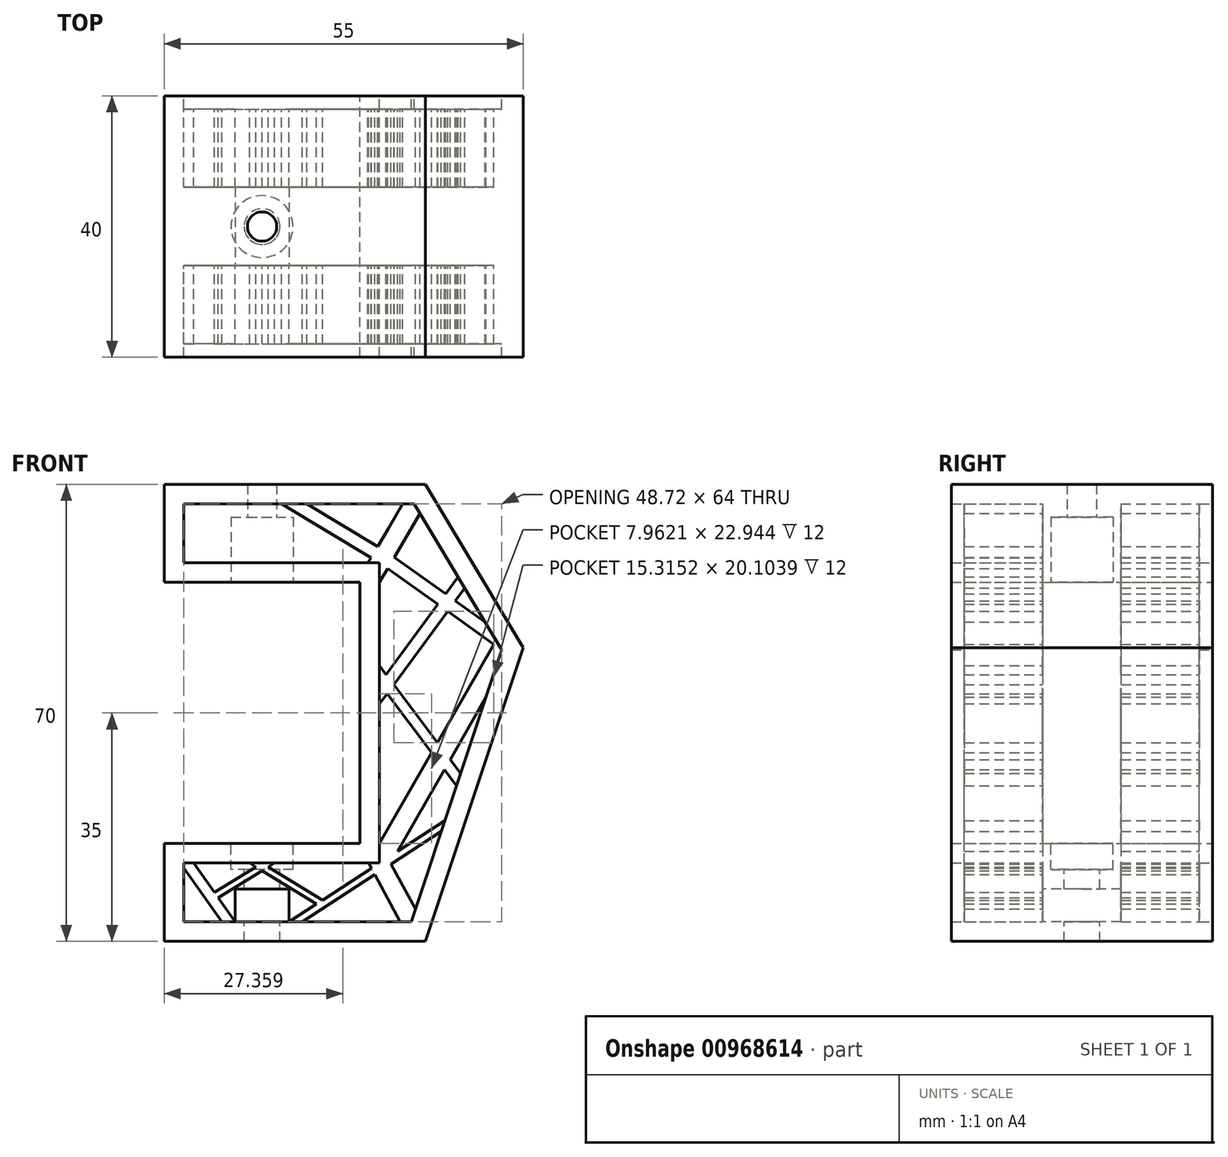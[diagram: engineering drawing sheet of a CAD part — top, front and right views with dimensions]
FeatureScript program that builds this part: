
annotation { "Feature Type Name" : "Feature", "Feature Type Description" : "" }
export const myFeature = defineFeature(function(context is Context, id is Id, definition is map)
    precondition{}
    {
        {
            var Q0;
            Q0=qCreatedBy(makeId("Front.planeOp"),FACE);
            var sketch = newSketch(context, id + "F0", { "sketchPlane" : qUnion([Q0])});
            skLineSegment(sketch, "E0", {"start": v(0, 21.86) * mm, "end": v(-30, 21.86) * mm});
            skLineSegment(sketch, "E1", {"start": v(-30, 21.86) * mm, "end": v(-30, 36.86) * mm});
            skLineSegment(sketch, "E2", {"start": v(-30, 36.86) * mm, "end": v(10, 36.86) * mm});
            skLineSegment(sketch, "E3", {"start": v(0, -33.14) * mm, "end": v(-30, -33.14) * mm});
            skLineSegment(sketch, "E4", {"start": v(-30, -33.14) * mm, "end": v(-30, -18.14) * mm});
            skLineSegment(sketch, "E5", {"start": v(-30, -18.14) * mm, "end": v(0, -18.14) * mm});
            skLineSegment(sketch, "E6", {"start": v(0, -18.14) * mm, "end": v(0, 21.86) * mm});
            skLineSegment(sketch, "E7", {"start": v(10, -33.14) * mm, "end": v(0, -33.14) * mm});
            skLineSegment(sketch, "E8", {"start": v(10, 36.86) * mm, "end": v(25, 11.86) * mm});
            skLineSegment(sketch, "E9", {"start": v(25, 11.86) * mm, "end": v(10, -33.14) * mm});
            skPoint(sketch, "E10", {"position": v(-15, 21.86) * mm});
            skPoint(sketch, "E11", {"position": v(-15, -18.14) * mm});
            skLineSegment(sketch, "E12", {"start": v(0, 21.86) * mm, "end": v(0, 36.86) * mm});
            skLineSegment(sketch, "E13", {"start": v(0, -18.14) * mm, "end": v(0, -33.14) * mm});
            skLineSegment(sketch, "E14", {"start": v(-30, -18.14) * mm, "end": v(10, -33.14) * mm});
            skLineSegment(sketch, "E15", {"start": v(10, -33.14) * mm, "end": v(0, -18.14) * mm});
            skLineSegment(sketch, "E16", {"start": v(25, 11.86) * mm, "end": v(0, -18.14) * mm});
            skLineSegment(sketch, "E17", {"start": v(10, 36.86) * mm, "end": v(0, 21.86) * mm});
            skLineSegment(sketch, "E18", {"start": v(25, 11.86) * mm, "end": v(0, 21.86) * mm});
            skLineSegment(sketch, "E19", {"start": v(10, 36.86) * mm, "end": v(-30, 21.86) * mm});
            skLineSegment(sketch, "E20", {"start": v(-30, 36.86) * mm, "end": v(0, 21.86) * mm});
            skLineSegment(sketch, "E21", {"start": v(-30, -33.14) * mm, "end": v(0, -18.14) * mm});
            skSolve(sketch);
        }
        {
            var Q0;
            Q0 = qSketchRegion(id + "F0", true);
            extrude(context, id + "F1", {"entities" : qUnion([Q0]), "depth" : 20 * mm, "offsetDistance" : 25 * mm, "hasSecondDirection" : true, "secondDirectionOppositeDirection" : true, "secondDirectionDepth" : 20 * mm});
        }
        {
            var Q0;
            Q0=makeQuery(id+"F1.opExtrude","CAP_FACE",FACE,{"disambiguationData":[OSD([sQuery(id+"F0.wireOp",EDGE,"E0"),sQuery(id+"F0.wireOp",EDGE,"E1"),sQuery(id+"F0.wireOp",EDGE,"E2"),sQuery(id+"F0.wireOp",EDGE,"E3"),sQuery(id+"F0.wireOp",EDGE,"E4"),sQuery(id+"F0.wireOp",EDGE,"E5"),sQuery(id+"F0.wireOp",EDGE,"E6"),sQuery(id+"F0.wireOp",EDGE,"E7"),sQuery(id+"F0.wireOp",EDGE,"E8"),sQuery(id+"F0.wireOp",EDGE,"E9")])],"isStart":false});
            var Q1;
            Q1=makeQuery(id+"F1.opExtrude","CAP_FACE",FACE,{"disambiguationData":[OSD([sQuery(id+"F0.wireOp",EDGE,"E0"),sQuery(id+"F0.wireOp",EDGE,"E1"),sQuery(id+"F0.wireOp",EDGE,"E2"),sQuery(id+"F0.wireOp",EDGE,"E3"),sQuery(id+"F0.wireOp",EDGE,"E4"),sQuery(id+"F0.wireOp",EDGE,"E5"),sQuery(id+"F0.wireOp",EDGE,"E6"),sQuery(id+"F0.wireOp",EDGE,"E7"),sQuery(id+"F0.wireOp",EDGE,"E8"),sQuery(id+"F0.wireOp",EDGE,"E9")])],"isStart":true});
            shell(context, id + "F2", {"entities" : qUnion([Q0, Q1]), "thickness" : 3 * mm});
        }
        {
            var Q0;
            Q0 = qSketchRegion(id + "F0", true);
            extrude(context, id + "F3", {"entities" : qUnion([Q0]), "operationType" : NewBodyOperationType.ADD, "depth" : 6 * mm, "offsetDistance" : 25 * mm, "hasSecondDirection" : true, "secondDirectionOppositeDirection" : true, "secondDirectionDepth" : 6 * mm});
        }
        {
            var Q0;
            Q0=makeQuery(id+"F3.opExtrude","CAP_FACE",FACE,{"disambiguationData":[OSD([sQuery(id+"F0.wireOp",EDGE,"E0"),sQuery(id+"F0.wireOp",EDGE,"E1"),sQuery(id+"F0.wireOp",EDGE,"E2"),sQuery(id+"F0.wireOp",EDGE,"E3"),sQuery(id+"F0.wireOp",EDGE,"E4"),sQuery(id+"F0.wireOp",EDGE,"E5"),sQuery(id+"F0.wireOp",EDGE,"E6"),sQuery(id+"F0.wireOp",EDGE,"E7"),sQuery(id+"F0.wireOp",EDGE,"E8"),sQuery(id+"F0.wireOp",EDGE,"E9")])],"isStart":false});
            var sketch = newSketch(context, id + "F4", { "sketchPlane" : qUnion([Q0])});
            skLineSegment(sketch, "E22.bottom", {"start": v(-27, -21.14) * mm, "end": v(7.84, -21.14) * mm});
            skLineSegment(sketch, "E22.top", {"start": v(-27, -30.14) * mm, "end": v(7.84, -30.14) * mm});
            skLineSegment(sketch, "E22.left", {"start": v(-27, -21.14) * mm, "end": v(-27, -30.14) * mm});
            skLineSegment(sketch, "E22.right", {"start": v(7.84, -21.14) * mm, "end": v(7.84, -30.14) * mm});
            skLineSegment(sketch, "E23", {"start": v(-15, -30.14) * mm, "end": v(-15, -21.14) * mm});
            skLineSegment(sketch, "E24", {"start": v(-19.15, -25.14) * mm, "end": v(-10.85, -25.14) * mm});
            skLineSegment(sketch, "E25", {"start": v(-19.15, -25.14) * mm, "end": v(-19.15, -30.14) * mm});
            skLineSegment(sketch, "E26", {"start": v(-10.85, -25.14) * mm, "end": v(-10.85, -30.14) * mm});
            skLineSegment(sketch, "E27", {"start": v(-19.15, -30.14) * mm, "end": v(-25.5, -21.14) * mm});
            skLineSegment(sketch, "E28", {"start": v(-21.15, -30.14) * mm, "end": v(-27, -21.85) * mm});
            skLineSegment(sketch, "E29", {"start": v(-27, -21.85) * mm, "end": v(-27, -21.14) * mm});
            skLineSegment(sketch, "E30", {"start": v(-21.15, -30.14) * mm, "end": v(-19.15, -30.14) * mm});
            skLineSegment(sketch, "E31", {"start": v(-10.85, -30.14) * mm, "end": v(3, -21.14) * mm});
            skLineSegment(sketch, "E32", {"start": v(-22.32, -25.64) * mm, "end": v(-15, -21.14) * mm});
            skLineSegment(sketch, "E33", {"start": v(-21.75, -26.46) * mm, "end": v(-13.1, -21.14) * mm});
            skPoint(sketch, "E34", {"position": v(-8.85, -30.14) * mm});
            skLineSegment(sketch, "E35", {"start": v(-8.85, -30.14) * mm, "end": v(12.45, -16.3) * mm});
            skPoint(sketch, "E36", {"position": v(-16.9, -21.14) * mm});
            skLineSegment(sketch, "E37.MirrorCS", {"start": v(-7.68, -25.64) * mm, "end": v(-15, -21.14) * mm});
            skLineSegment(sketch, "E38", {"start": v(-16.9, -21.14) * mm, "end": v(-6.67, -27.43) * mm});
            skLineSegment(sketch, "E39", {"start": v(-15, -21.14) * mm, "end": v(-5.75, -26.82) * mm});
            skLineSegment(sketch, "E40.bottom", {"start": v(3, -21.14) * mm, "end": v(8.3, -21.14) * mm});
            skLineSegment(sketch, "E40.top", {"start": v(3, 33.86) * mm, "end": v(8.3, 33.86) * mm});
            skLineSegment(sketch, "E40.left", {"start": v(3, -21.14) * mm, "end": v(3, 33.86) * mm});
            skLineSegment(sketch, "E40.right", {"start": v(8.3, -21.14) * mm, "end": v(8.3, 33.86) * mm});
            skLineSegment(sketch, "E41.bottom", {"start": v(-27, 33.86) * mm, "end": v(3, 33.86) * mm});
            skLineSegment(sketch, "E41.top", {"start": v(-27, 24.86) * mm, "end": v(3, 24.86) * mm});
            skLineSegment(sketch, "E41.left", {"start": v(-27, 33.86) * mm, "end": v(-27, 24.86) * mm});
            skLineSegment(sketch, "E41.right", {"start": v(3, 33.86) * mm, "end": v(3, 24.86) * mm});
            skLineSegment(sketch, "E42.bottom", {"start": v(8.3, 33.86) * mm, "end": v(21.72, 33.86) * mm});
            skLineSegment(sketch, "E42.top", {"start": v(8.3, 11.5) * mm, "end": v(21.72, 11.5) * mm});
            skLineSegment(sketch, "E42.left", {"start": v(8.3, 33.86) * mm, "end": v(8.3, 11.5) * mm});
            skLineSegment(sketch, "E42.right", {"start": v(21.72, 33.86) * mm, "end": v(21.72, 11.5) * mm});
            skLineSegment(sketch, "E43.bottom", {"start": v(7.84, -30.14) * mm, "end": v(21.72, -30.14) * mm});
            skLineSegment(sketch, "E43.top", {"start": v(7.84, 11.5) * mm, "end": v(21.72, 11.5) * mm});
            skLineSegment(sketch, "E43.left", {"start": v(7.84, -30.14) * mm, "end": v(7.84, 11.5) * mm});
            skLineSegment(sketch, "E43.right", {"start": v(21.72, -30.14) * mm, "end": v(21.72, 11.5) * mm});
            skLineSegment(sketch, "E44", {"start": v(3, -21.14) * mm, "end": v(13, -14.64) * mm});
            skLineSegment(sketch, "E45", {"start": v(3, 6.36) * mm, "end": v(15, 22.68) * mm});
            skLineSegment(sketch, "E46", {"start": v(3, 6.36) * mm, "end": v(14.78, -9.32) * mm});
            skLineSegment(sketch, "E47", {"start": v(3, 9.1) * mm, "end": v(15.41, -7.42) * mm});
            skLineSegment(sketch, "E48", {"start": v(3, 3.25) * mm, "end": v(16.04, 20.96) * mm});
            skLineSegment(sketch, "E49", {"start": v(21.72, 11.5) * mm, "end": v(3, -21.14) * mm});
            skLineSegment(sketch, "E50", {"start": v(3, -21.14) * mm, "end": v(7.84, -30.14) * mm});
            skLineSegment(sketch, "E51", {"start": v(5.76, -19.35) * mm, "end": v(19.32, 4.3) * mm});
            skLineSegment(sketch, "E52", {"start": v(3, -18.13) * mm, "end": v(20.83, 12.97) * mm});
            skLineSegment(sketch, "E53", {"start": v(5.89, -8.16) * mm, "end": v(12.43, -11.91) * mm});
            skPoint(sketch, "E54", {"position": v(9.32, -10.13) * mm});
            skPoint(sketch, "E55", {"position": v(10.62, -10.87) * mm});
            skPoint(sketch, "E56", {"position": v(8.01, -9.38) * mm});
            skPoint(sketch, "E57", {"position": v(5.2, -25.23) * mm});
            skPoint(sketch, "E58", {"position": v(3.87, -25.93) * mm});
            skLineSegment(sketch, "E59", {"start": v(3.87, -25.93) * mm, "end": v(7.4, -24.03) * mm});
            skPoint(sketch, "E60", {"position": v(6.51, -24.5) * mm});
            skLineSegment(sketch, "E61", {"start": v(3.87, -25.93) * mm, "end": v(1.3, -21.14) * mm});
            skPoint(sketch, "E62", {"position": v(1.3, -21.14) * mm});
            skLineSegment(sketch, "E63", {"start": v(6.51, -24.5) * mm, "end": v(4.78, -21.28) * mm});
            skLineSegment(sketch, "E64", {"start": v(3.87, -25.93) * mm, "end": v(6.13, -30.14) * mm});
            skLineSegment(sketch, "E65", {"start": v(6.51, -24.5) * mm, "end": v(8.49, -28.19) * mm});
            skLineSegment(sketch, "E66", {"start": v(21.72, 11.5) * mm, "end": v(3, 24.86) * mm});
            skLineSegment(sketch, "E67", {"start": v(3, 24.86) * mm, "end": v(-12, 33.86) * mm});
            skLineSegment(sketch, "E68", {"start": v(3, 24.86) * mm, "end": v(4.16, 26.49) * mm});
            skLineSegment(sketch, "E69", {"start": v(4.16, 26.49) * mm, "end": v(-8.12, 33.86) * mm});
            skLineSegment(sketch, "E70", {"start": v(4.16, 26.49) * mm, "end": v(19.14, 15.8) * mm});
            skLineSegment(sketch, "E71", {"start": v(8.3, 33.86) * mm, "end": v(3, 24.86) * mm});
            skLineSegment(sketch, "E72", {"start": v(5.65, 29.36) * mm, "end": v(4.36, 30.12) * mm});
            skLineSegment(sketch, "E73", {"start": v(5.65, 29.36) * mm, "end": v(6.94, 28.6) * mm});
            skLineSegment(sketch, "E74", {"start": v(4.36, 30.12) * mm, "end": v(6.56, 33.86) * mm});
            skLineSegment(sketch, "E75", {"start": v(6.94, 28.6) * mm, "end": v(3, 21.9) * mm});
            skLineSegment(sketch, "E76", {"start": v(6.94, 28.6) * mm, "end": v(9.18, 32.4) * mm});
            skLineSegment(sketch, "E77", {"start": v(4.36, 30.12) * mm, "end": v(1.2, 24.86) * mm});
            skSolve(sketch);
        }
        {
            var Q0;
            {var subQ3=sQuery(id+"F4.wireOp",EDGE,"E25");Q0=makeQuery(id+"F4.imprint","IMPRINT",FACE,{"disambiguationData":[TD([[makeQuery(id+"F4.imprint","IMPRINT",EDGE,{"derivedFrom":subQ3}),1.0]])]});}
            var Q1;
            {var subQ3=sQuery(id+"F4.wireOp",EDGE,"E26");Q1=makeQuery(id+"F4.imprint","IMPRINT",FACE,{"disambiguationData":[TD([[makeQuery(id+"F4.imprint","IMPRINT",EDGE,{"derivedFrom":subQ3}),-1.0]])]});}
            extrude(context, id + "F5", {"entities" : qUnion([Q0, Q1]), "operationType" : NewBodyOperationType.REMOVE, "oppositeDirection" : true, "depth" : 15 * mm, "offsetDistance" : 25 * mm});
        }
        {
            var Q0;
            {var subQ6=sQuery(id+"F4.wireOp",EDGE,"E28");Q0=makeQuery(id+"F4.imprint","IMPRINT",FACE,{"disambiguationData":[TD([[makeQuery(id+"F4.imprint","IMPRINT",EDGE,{"derivedFrom":subQ6}),-1.0]])]});}
            var Q1;
            {var subQ0=sQuery(id+"F4.wireOp",EDGE,"E32");var subQ1=sQuery(id+"F4.wireOp",EDGE,"E27");var subQ2=makeQuery(id+"F4.imprint","INTERSECT",VERTEX,{"derivedFrom":[subQ1,subQ0]});Q1=makeQuery(id+"F4.imprint","IMPRINT",FACE,{"disambiguationData":[TD([[makeQuery(id+"F4.imprint","IMPRINT",EDGE,{"disambiguationData":[TD([[subQ2,1.0]])],"derivedFrom":subQ1}),-1.0]])]});}
            var Q2;
            {var subQ0=sQuery(id+"F4.wireOp",EDGE,"E32");var subQ3=sQuery(id+"F4.wireOp",EDGE,"E38");var subQ5=makeQuery(id+"F4.imprint","INTERSECT",VERTEX,{"derivedFrom":[subQ0,subQ3]});Q2=makeQuery(id+"F4.imprint","IMPRINT",FACE,{"disambiguationData":[TD([[makeQuery(id+"F4.imprint","IMPRINT",EDGE,{"disambiguationData":[TD([[subQ5,-1.0]])],"derivedFrom":subQ3}),1.0]])]});}
            var Q3;
            {var subQ0=sQuery(id+"F4.wireOp",EDGE,"E37.MirrorCS");var subQ3=sQuery(id+"F4.wireOp",EDGE,"E33");var subQ5=makeQuery(id+"F4.imprint","INTERSECT",VERTEX,{"derivedFrom":[subQ3,subQ0]});Q3=makeQuery(id+"F4.imprint","IMPRINT",FACE,{"disambiguationData":[TD([[makeQuery(id+"F4.imprint","IMPRINT",EDGE,{"disambiguationData":[TD([[subQ5,1.0]])],"derivedFrom":subQ3}),1.0]])]});}
            var Q4;
            {var subQ1=sQuery(id+"F4.wireOp",EDGE,"E22.bottom");var subQ3=sQuery(id+"F4.wireOp",EDGE,"E38");var subQ4=makeQuery(id+"F4.imprint","INTERSECT",VERTEX,{"derivedFrom":[subQ1,subQ3]});Q4=makeQuery(id+"F4.imprint","IMPRINT",FACE,{"disambiguationData":[TD([[makeQuery(id+"F4.imprint","IMPRINT",EDGE,{"disambiguationData":[TD([[subQ4,-1.0]])],"derivedFrom":subQ3}),1.0]])]});}
            var Q5;
            {var subQ0=sQuery(id+"F4.wireOp",EDGE,"E37.MirrorCS");var subQ3=sQuery(id+"F4.wireOp",EDGE,"E33");var subQ5=makeQuery(id+"F4.imprint","INTERSECT",VERTEX,{"derivedFrom":[subQ3,subQ0]});Q5=makeQuery(id+"F4.imprint","IMPRINT",FACE,{"disambiguationData":[TD([[makeQuery(id+"F4.imprint","IMPRINT",EDGE,{"disambiguationData":[TD([[subQ5,-1.0]])],"derivedFrom":subQ3}),1.0]])]});}
            var Q6;
            {var subQ3=sQuery(id+"F4.wireOp",EDGE,"E39");Q6=makeQuery(id+"F4.imprint","IMPRINT",FACE,{"disambiguationData":[TD([[makeQuery(id+"F4.imprint","IMPRINT",EDGE,{"derivedFrom":subQ3}),-1.0]])]});}
            var Q7;
            {var subQ0=sQuery(id+"F4.wireOp",EDGE,"E31");var subQ1=makeQuery(id+"F4.imprint","INTERSECT",VERTEX,{"derivedFrom":[subQ0,sQuery(id+"F4.wireOp",EDGE,"E39")]});Q7=makeQuery(id+"F4.imprint","IMPRINT",FACE,{"disambiguationData":[TD([[makeQuery(id+"F4.imprint","IMPRINT",EDGE,{"disambiguationData":[TD([[subQ1,-1.0]])],"derivedFrom":subQ0}),-1.0]])]});}
            var Q8;
            {var subQ4=sQuery(id+"F4.wireOp",EDGE,"E64");Q8=makeQuery(id+"F4.imprint","IMPRINT",FACE,{"disambiguationData":[TD([[makeQuery(id+"F4.imprint","IMPRINT",EDGE,{"derivedFrom":subQ4}),1.0]])]});}
            var Q9;
            {var subQ0=sQuery(id+"F4.wireOp",EDGE,"E50");var subQ6=sQuery(id+"F4.wireOp",EDGE,"E59");var subQ7=makeQuery(id+"F4.imprint","INTERSECT",VERTEX,{"derivedFrom":[subQ0,subQ6]});Q9=makeQuery(id+"F4.imprint","IMPRINT",FACE,{"disambiguationData":[TD([[makeQuery(id+"F4.imprint","IMPRINT",EDGE,{"disambiguationData":[TD([[subQ7,-1.0]])],"derivedFrom":subQ6}),-1.0]])]});}
            var Q10;
            {var subQ0=sQuery(id+"F4.wireOp",EDGE,"E22.right");var subQ4=sQuery(id+"F4.wireOp",EDGE,"E65");var subQ5=makeQuery(id+"F4.imprint","INTERSECT",VERTEX,{"derivedFrom":[subQ0,subQ4]});Q10=makeQuery(id+"F4.imprint","IMPRINT",FACE,{"disambiguationData":[TD([[makeQuery(id+"F4.imprint","IMPRINT",EDGE,{"disambiguationData":[TD([[subQ5,-1.0]])],"derivedFrom":subQ4}),-1.0]])]});}
            var Q11;
            {var subQ3=sQuery(id+"F4.wireOp",EDGE,"E63");Q11=makeQuery(id+"F4.imprint","IMPRINT",FACE,{"disambiguationData":[TD([[makeQuery(id+"F4.imprint","IMPRINT",EDGE,{"derivedFrom":subQ3}),1.0]])]});}
            var Q12;
            {var subQ0=sQuery(id+"F4.wireOp",EDGE,"E50");var subQ1=sQuery(id+"F4.wireOp",EDGE,"E35");var subQ2=makeQuery(id+"F4.imprint","INTERSECT",VERTEX,{"derivedFrom":[subQ1,subQ0]});Q12=makeQuery(id+"F4.imprint","IMPRINT",FACE,{"disambiguationData":[TD([[makeQuery(id+"F4.imprint","IMPRINT",EDGE,{"disambiguationData":[TD([[subQ2,1.0]])],"derivedFrom":subQ1}),-1.0]])]});}
            var Q13;
            {var subQ1=sQuery(id+"F4.wireOp",EDGE,"E22.bottom");var subQ3=sQuery(id+"F4.wireOp",EDGE,"E61");var subQ4=makeQuery(id+"F4.imprint","INTERSECT",VERTEX,{"derivedFrom":[subQ1,subQ3]});Q13=makeQuery(id+"F4.imprint","IMPRINT",FACE,{"disambiguationData":[TD([[makeQuery(id+"F4.imprint","IMPRINT",EDGE,{"disambiguationData":[TD([[subQ4,1.0]])],"derivedFrom":subQ3}),-1.0]])]});}
            var Q14;
            {var subQ0=sQuery(id+"F4.wireOp",EDGE,"E50");var subQ5=sQuery(id+"F4.wireOp",EDGE,"E35");var subQ6=makeQuery(id+"F4.imprint","INTERSECT",VERTEX,{"derivedFrom":[subQ5,subQ0]});Q14=makeQuery(id+"F4.imprint","IMPRINT",FACE,{"disambiguationData":[TD([[makeQuery(id+"F4.imprint","IMPRINT",EDGE,{"disambiguationData":[TD([[subQ6,1.0]])],"derivedFrom":subQ5}),1.0]])]});}
            var Q15;
            {var subQ0=sQuery(id+"F4.wireOp",EDGE,"E50");var subQ3=sQuery(id+"F4.wireOp",EDGE,"E35");var subQ5=makeQuery(id+"F4.imprint","INTERSECT",VERTEX,{"derivedFrom":[subQ3,subQ0]});Q15=makeQuery(id+"F4.imprint","IMPRINT",FACE,{"disambiguationData":[TD([[makeQuery(id+"F4.imprint","IMPRINT",EDGE,{"disambiguationData":[TD([[subQ5,-1.0]])],"derivedFrom":subQ3}),1.0]])]});}
            var Q16;
            {var subQ1=sQuery(id+"F4.wireOp",EDGE,"E35");var subQ5=sQuery(id+"F4.wireOp",EDGE,"E22.bottom");var subQ6=makeQuery(id+"F4.imprint","INTERSECT",VERTEX,{"derivedFrom":[subQ5,subQ1]});Q16=makeQuery(id+"F4.imprint","IMPRINT",FACE,{"disambiguationData":[TD([[makeQuery(id+"F4.imprint","IMPRINT",EDGE,{"disambiguationData":[TD([[subQ6,-1.0]])],"derivedFrom":subQ1}),1.0]])]});}
            var Q17;
            {var subQ0=sQuery(id+"F4.wireOp",EDGE,"E49");var subQ1=sQuery(id+"F4.wireOp",EDGE,"E43.left");var subQ2=makeQuery(id+"F4.imprint","INTERSECT",VERTEX,{"derivedFrom":[subQ1,subQ0]});Q17=makeQuery(id+"F4.imprint","IMPRINT",FACE,{"disambiguationData":[TD([[makeQuery(id+"F4.imprint","IMPRINT",EDGE,{"disambiguationData":[TD([[subQ2,1.0]])],"derivedFrom":subQ1}),1.0]])]});}
            var Q18;
            {var subQ0=sQuery(id+"F4.wireOp",EDGE,"E49");var subQ5=sQuery(id+"F4.wireOp",EDGE,"E43.left");var subQ6=makeQuery(id+"F4.imprint","INTERSECT",VERTEX,{"derivedFrom":[subQ5,subQ0]});Q18=makeQuery(id+"F4.imprint","IMPRINT",FACE,{"disambiguationData":[TD([[makeQuery(id+"F4.imprint","IMPRINT",EDGE,{"disambiguationData":[TD([[subQ6,-1.0]])],"derivedFrom":subQ5}),1.0]])]});}
            var Q19;
            {var subQ0=sQuery(id+"F4.wireOp",EDGE,"E40.right");var subQ1=sQuery(id+"F4.wireOp",EDGE,"E35");var subQ2=makeQuery(id+"F4.imprint","INTERSECT",VERTEX,{"derivedFrom":[subQ1,subQ0]});Q19=makeQuery(id+"F4.imprint","IMPRINT",FACE,{"disambiguationData":[TD([[makeQuery(id+"F4.imprint","IMPRINT",EDGE,{"disambiguationData":[TD([[subQ2,1.0]])],"derivedFrom":subQ1}),1.0]])]});}
            var Q20;
            {var subQ0=sQuery(id+"F4.wireOp",EDGE,"E40.right");var subQ6=sQuery(id+"F4.wireOp",EDGE,"E44");var subQ7=makeQuery(id+"F4.imprint","INTERSECT",VERTEX,{"derivedFrom":[subQ0,subQ6]});Q20=makeQuery(id+"F4.imprint","IMPRINT",FACE,{"disambiguationData":[TD([[makeQuery(id+"F4.imprint","IMPRINT",EDGE,{"disambiguationData":[TD([[subQ7,1.0]])],"derivedFrom":subQ0}),-1.0]])]});}
            var Q21;
            {var subQ0=sQuery(id+"F4.wireOp",EDGE,"E51");var subQ1=sQuery(id+"F4.wireOp",EDGE,"E40.right");var subQ2=makeQuery(id+"F4.imprint","INTERSECT",VERTEX,{"derivedFrom":[subQ1,subQ0]});Q21=makeQuery(id+"F4.imprint","IMPRINT",FACE,{"disambiguationData":[TD([[makeQuery(id+"F4.imprint","IMPRINT",EDGE,{"disambiguationData":[TD([[subQ2,-1.0]])],"derivedFrom":subQ1}),1.0]])]});}
            var Q22;
            {var subQ5=sQuery(id+"F4.wireOp",EDGE,"E49");var subQ7=sQuery(id+"F4.wireOp",EDGE,"E40.right");var subQ8=makeQuery(id+"F4.imprint","INTERSECT",VERTEX,{"derivedFrom":[subQ7,subQ5]});Q22=makeQuery(id+"F4.imprint","IMPRINT",FACE,{"disambiguationData":[TD([[makeQuery(id+"F4.imprint","IMPRINT",EDGE,{"disambiguationData":[TD([[subQ8,-1.0]])],"derivedFrom":subQ7}),1.0]])]});}
            var Q23;
            {var subQ0=sQuery(id+"F4.wireOp",EDGE,"E49");var subQ1=sQuery(id+"F4.wireOp",EDGE,"E40.right");var subQ2=makeQuery(id+"F4.imprint","INTERSECT",VERTEX,{"derivedFrom":[subQ1,subQ0]});Q23=makeQuery(id+"F4.imprint","IMPRINT",FACE,{"disambiguationData":[TD([[makeQuery(id+"F4.imprint","IMPRINT",EDGE,{"disambiguationData":[TD([[subQ2,-1.0]])],"derivedFrom":subQ1}),-1.0]])]});}
            var Q24;
            {var subQ0=sQuery(id+"F4.wireOp",EDGE,"E51");var subQ1=sQuery(id+"F4.wireOp",EDGE,"E40.right");var subQ2=makeQuery(id+"F4.imprint","INTERSECT",VERTEX,{"derivedFrom":[subQ1,subQ0]});Q24=makeQuery(id+"F4.imprint","IMPRINT",FACE,{"disambiguationData":[TD([[makeQuery(id+"F4.imprint","IMPRINT",EDGE,{"disambiguationData":[TD([[subQ2,-1.0]])],"derivedFrom":subQ1}),-1.0]])]});}
            var Q25;
            {var subQ0=sQuery(id+"F4.wireOp",EDGE,"E51");var subQ1=sQuery(id+"F4.wireOp",EDGE,"E46");var subQ2=makeQuery(id+"F4.imprint","INTERSECT",VERTEX,{"derivedFrom":[subQ1,subQ0]});Q25=makeQuery(id+"F4.imprint","IMPRINT",FACE,{"disambiguationData":[TD([[makeQuery(id+"F4.imprint","IMPRINT",EDGE,{"disambiguationData":[TD([[subQ2,1.0]])],"derivedFrom":subQ1}),-1.0]])]});}
            var Q26;
            {var subQ0=sQuery(id+"F4.wireOp",EDGE,"E52");var subQ1=sQuery(id+"F4.wireOp",EDGE,"E40.right");var subQ2=makeQuery(id+"F4.imprint","INTERSECT",VERTEX,{"derivedFrom":[subQ1,subQ0]});Q26=makeQuery(id+"F4.imprint","IMPRINT",FACE,{"disambiguationData":[TD([[makeQuery(id+"F4.imprint","IMPRINT",EDGE,{"disambiguationData":[TD([[subQ2,1.0]])],"derivedFrom":subQ1}),-1.0]])]});}
            var Q27;
            {var subQ0=sQuery(id+"F4.wireOp",EDGE,"E52");var subQ1=sQuery(id+"F4.wireOp",EDGE,"E40.right");var subQ2=makeQuery(id+"F4.imprint","INTERSECT",VERTEX,{"derivedFrom":[subQ1,subQ0]});Q27=makeQuery(id+"F4.imprint","IMPRINT",FACE,{"disambiguationData":[TD([[makeQuery(id+"F4.imprint","IMPRINT",EDGE,{"disambiguationData":[TD([[subQ2,1.0]])],"derivedFrom":subQ1}),1.0]])]});}
            var Q28;
            {var subQ0=sQuery(id+"F4.wireOp",EDGE,"E51");var subQ6=sQuery(id+"F4.wireOp",EDGE,"E47");var subQ7=makeQuery(id+"F4.imprint","INTERSECT",VERTEX,{"derivedFrom":[subQ6,subQ0]});Q28=makeQuery(id+"F4.imprint","IMPRINT",FACE,{"disambiguationData":[TD([[makeQuery(id+"F4.imprint","IMPRINT",EDGE,{"disambiguationData":[TD([[subQ7,1.0]])],"derivedFrom":subQ0}),-1.0]])]});}
            var Q29;
            {var subQ0=sQuery(id+"F4.wireOp",EDGE,"E51");var subQ1=sQuery(id+"F4.wireOp",EDGE,"E46");var subQ2=makeQuery(id+"F4.imprint","INTERSECT",VERTEX,{"derivedFrom":[subQ1,subQ0]});Q29=makeQuery(id+"F4.imprint","IMPRINT",FACE,{"disambiguationData":[TD([[makeQuery(id+"F4.imprint","IMPRINT",EDGE,{"disambiguationData":[TD([[subQ2,1.0]])],"derivedFrom":subQ1}),1.0]])]});}
            var Q30;
            {var subQ0=sQuery(id+"F4.wireOp",EDGE,"E52");var subQ1=sQuery(id+"F4.wireOp",EDGE,"E46");var subQ2=makeQuery(id+"F4.imprint","INTERSECT",VERTEX,{"derivedFrom":[subQ1,subQ0]});Q30=makeQuery(id+"F4.imprint","IMPRINT",FACE,{"disambiguationData":[TD([[makeQuery(id+"F4.imprint","IMPRINT",EDGE,{"disambiguationData":[TD([[subQ2,-1.0]])],"derivedFrom":subQ1}),1.0]])]});}
            var Q31;
            {var subQ0=sQuery(id+"F4.wireOp",EDGE,"E47");var subQ1=sQuery(id+"F4.wireOp",EDGE,"E40.right");var subQ2=makeQuery(id+"F4.imprint","INTERSECT",VERTEX,{"derivedFrom":[subQ1,subQ0]});Q31=makeQuery(id+"F4.imprint","IMPRINT",FACE,{"disambiguationData":[TD([[makeQuery(id+"F4.imprint","IMPRINT",EDGE,{"disambiguationData":[TD([[subQ2,1.0]])],"derivedFrom":subQ1}),-1.0]])]});}
            var Q32;
            {var subQ6=sQuery(id+"F4.wireOp",EDGE,"E52");var subQ8=sQuery(id+"F4.wireOp",EDGE,"E47");var subQ9=makeQuery(id+"F4.imprint","INTERSECT",VERTEX,{"derivedFrom":[subQ8,subQ6]});Q32=makeQuery(id+"F4.imprint","IMPRINT",FACE,{"disambiguationData":[TD([[makeQuery(id+"F4.imprint","IMPRINT",EDGE,{"disambiguationData":[TD([[subQ9,-1.0]])],"derivedFrom":subQ8}),1.0]])]});}
            var Q33;
            {var subQ0=sQuery(id+"F4.wireOp",EDGE,"E51");var subQ1=sQuery(id+"F4.wireOp",EDGE,"E47");var subQ2=makeQuery(id+"F4.imprint","INTERSECT",VERTEX,{"derivedFrom":[subQ1,subQ0]});Q33=makeQuery(id+"F4.imprint","IMPRINT",FACE,{"disambiguationData":[TD([[makeQuery(id+"F4.imprint","IMPRINT",EDGE,{"disambiguationData":[TD([[subQ2,1.0]])],"derivedFrom":subQ1}),1.0]])]});}
            var Q34;
            {var subQ0=sQuery(id+"F4.wireOp",EDGE,"E47");var subQ1=sQuery(id+"F4.wireOp",EDGE,"E40.right");var subQ2=makeQuery(id+"F4.imprint","INTERSECT",VERTEX,{"derivedFrom":[subQ1,subQ0]});Q34=makeQuery(id+"F4.imprint","IMPRINT",FACE,{"disambiguationData":[TD([[makeQuery(id+"F4.imprint","IMPRINT",EDGE,{"disambiguationData":[TD([[subQ2,1.0]])],"derivedFrom":subQ1}),1.0]])]});}
            var Q35;
            {var subQ0=sQuery(id+"F4.wireOp",EDGE,"E46");var subQ1=sQuery(id+"F4.wireOp",EDGE,"E43.left");var subQ2=makeQuery(id+"F4.imprint","INTERSECT",VERTEX,{"derivedFrom":[subQ1,subQ0]});Q35=makeQuery(id+"F4.imprint","IMPRINT",FACE,{"disambiguationData":[TD([[makeQuery(id+"F4.imprint","IMPRINT",EDGE,{"disambiguationData":[TD([[subQ2,-1.0]])],"derivedFrom":subQ1}),1.0]])]});}
            var Q36;
            {var subQ0=sQuery(id+"F4.wireOp",EDGE,"E48");var subQ3=sQuery(id+"F4.wireOp",EDGE,"E46");var subQ5=makeQuery(id+"F4.imprint","INTERSECT",VERTEX,{"derivedFrom":[subQ3,subQ0]});Q36=makeQuery(id+"F4.imprint","IMPRINT",FACE,{"disambiguationData":[TD([[makeQuery(id+"F4.imprint","IMPRINT",EDGE,{"disambiguationData":[TD([[subQ5,1.0]])],"derivedFrom":subQ0}),1.0]])]});}
            var Q37;
            {var subQ0=sQuery(id+"F4.wireOp",EDGE,"E47");var subQ1=sQuery(id+"F4.wireOp",EDGE,"E45");var subQ2=makeQuery(id+"F4.imprint","INTERSECT",VERTEX,{"derivedFrom":[subQ1,subQ0]});Q37=makeQuery(id+"F4.imprint","IMPRINT",FACE,{"disambiguationData":[TD([[makeQuery(id+"F4.imprint","IMPRINT",EDGE,{"disambiguationData":[TD([[subQ2,-1.0]])],"derivedFrom":subQ0}),-1.0]])]});}
            var Q38;
            {var subQ6=sQuery(id+"F4.wireOp",EDGE,"E43.top");Q38=makeQuery(id+"F4.imprint","IMPRINT",FACE,{"disambiguationData":[TD([[makeQuery(id+"F4.imprint","IMPRINT",EDGE,{"derivedFrom":subQ6}),1.0]])]});}
            var Q39;
            {var subQ0=sQuery(id+"F4.wireOp",EDGE,"E47");var subQ3=sQuery(id+"F4.wireOp",EDGE,"E45");var subQ5=makeQuery(id+"F4.imprint","INTERSECT",VERTEX,{"derivedFrom":[subQ3,subQ0]});Q39=makeQuery(id+"F4.imprint","IMPRINT",FACE,{"disambiguationData":[TD([[makeQuery(id+"F4.imprint","IMPRINT",EDGE,{"disambiguationData":[TD([[subQ5,1.0]])],"derivedFrom":subQ0}),-1.0]])]});}
            var Q40;
            {var subQ0=sQuery(id+"F4.wireOp",EDGE,"E43.top");Q40=makeQuery(id+"F4.imprint","IMPRINT",FACE,{"disambiguationData":[TD([[makeQuery(id+"F4.imprint","IMPRINT",EDGE,{"derivedFrom":subQ0}),-1.0]])]});}
            var Q41;
            {var subQ0=sQuery(id+"F4.wireOp",EDGE,"E42.top");var subQ3=sQuery(id+"F4.wireOp",EDGE,"E48");var subQ5=makeQuery(id+"F4.imprint","INTERSECT",VERTEX,{"derivedFrom":[subQ0,subQ3]});Q41=makeQuery(id+"F4.imprint","IMPRINT",FACE,{"disambiguationData":[TD([[makeQuery(id+"F4.imprint","IMPRINT",EDGE,{"disambiguationData":[TD([[subQ5,1.0]])],"derivedFrom":subQ3}),1.0]])]});}
            var Q42;
            {var subQ5=sQuery(id+"F4.wireOp",EDGE,"E45");var subQ6=sQuery(id+"F4.wireOp",EDGE,"E40.right");var subQ7=makeQuery(id+"F4.imprint","INTERSECT",VERTEX,{"derivedFrom":[subQ6,subQ5]});Q42=makeQuery(id+"F4.imprint","IMPRINT",FACE,{"disambiguationData":[TD([[makeQuery(id+"F4.imprint","IMPRINT",EDGE,{"disambiguationData":[TD([[subQ7,-1.0]])],"derivedFrom":subQ5}),-1.0]])]});}
            var Q43;
            {var subQ0=sQuery(id+"F4.wireOp",EDGE,"E66");var subQ6=sQuery(id+"F4.wireOp",EDGE,"E52");var subQ8=makeQuery(id+"F4.imprint","INTERSECT",VERTEX,{"derivedFrom":[subQ6,subQ0]});Q43=makeQuery(id+"F4.imprint","IMPRINT",FACE,{"disambiguationData":[TD([[makeQuery(id+"F4.imprint","IMPRINT",EDGE,{"disambiguationData":[TD([[subQ8,1.0]])],"derivedFrom":subQ6}),-1.0]])]});}
            var Q44;
            {var subQ0=sQuery(id+"F4.wireOp",EDGE,"E66");var subQ1=sQuery(id+"F4.wireOp",EDGE,"E52");var subQ2=makeQuery(id+"F4.imprint","INTERSECT",VERTEX,{"derivedFrom":[subQ1,subQ0]});Q44=makeQuery(id+"F4.imprint","IMPRINT",FACE,{"disambiguationData":[TD([[makeQuery(id+"F4.imprint","IMPRINT",EDGE,{"disambiguationData":[TD([[subQ2,-1.0]])],"derivedFrom":subQ1}),-1.0]])]});}
            var Q45;
            {var subQ0=sQuery(id+"F4.wireOp",EDGE,"E66");var subQ3=sQuery(id+"F4.wireOp",EDGE,"E48");var subQ4=makeQuery(id+"F4.imprint","INTERSECT",VERTEX,{"derivedFrom":[subQ3,subQ0]});Q45=makeQuery(id+"F4.imprint","IMPRINT",FACE,{"disambiguationData":[TD([[makeQuery(id+"F4.imprint","IMPRINT",EDGE,{"disambiguationData":[TD([[subQ4,-1.0]])],"derivedFrom":subQ3}),-1.0]])]});}
            var Q46;
            {var subQ0=sQuery(id+"F4.wireOp",EDGE,"E66");var subQ1=sQuery(id+"F4.wireOp",EDGE,"E45");var subQ2=makeQuery(id+"F4.imprint","INTERSECT",VERTEX,{"derivedFrom":[subQ1,subQ0]});Q46=makeQuery(id+"F4.imprint","IMPRINT",FACE,{"disambiguationData":[TD([[makeQuery(id+"F4.imprint","IMPRINT",EDGE,{"disambiguationData":[TD([[subQ2,-1.0]])],"derivedFrom":subQ1}),-1.0]])]});}
            var Q47;
            {var subQ0=sQuery(id+"F4.wireOp",EDGE,"E70");var subQ1=sQuery(id+"F4.wireOp",EDGE,"E45");var subQ2=makeQuery(id+"F4.imprint","INTERSECT",VERTEX,{"derivedFrom":[subQ1,subQ0]});Q47=makeQuery(id+"F4.imprint","IMPRINT",FACE,{"disambiguationData":[TD([[makeQuery(id+"F4.imprint","IMPRINT",EDGE,{"disambiguationData":[TD([[subQ2,-1.0]])],"derivedFrom":subQ0}),1.0]])]});}
            var Q48;
            {var subQ0=sQuery(id+"F4.wireOp",EDGE,"E70");var subQ1=sQuery(id+"F4.wireOp",EDGE,"E40.right");var subQ2=makeQuery(id+"F4.imprint","INTERSECT",VERTEX,{"derivedFrom":[subQ1,subQ0]});Q48=makeQuery(id+"F4.imprint","IMPRINT",FACE,{"disambiguationData":[TD([[makeQuery(id+"F4.imprint","IMPRINT",EDGE,{"disambiguationData":[TD([[subQ2,1.0]])],"derivedFrom":subQ1}),-1.0]])]});}
            var Q49;
            {var subQ0=sQuery(id+"F4.wireOp",EDGE,"E70");var subQ1=sQuery(id+"F4.wireOp",EDGE,"E40.right");var subQ2=makeQuery(id+"F4.imprint","INTERSECT",VERTEX,{"derivedFrom":[subQ1,subQ0]});Q49=makeQuery(id+"F4.imprint","IMPRINT",FACE,{"disambiguationData":[TD([[makeQuery(id+"F4.imprint","IMPRINT",EDGE,{"disambiguationData":[TD([[subQ2,1.0]])],"derivedFrom":subQ1}),1.0]])]});}
            var Q50;
            {var subQ6=sQuery(id+"F4.wireOp",EDGE,"E73");Q50=makeQuery(id+"F4.imprint","IMPRINT",FACE,{"disambiguationData":[TD([[makeQuery(id+"F4.imprint","IMPRINT",EDGE,{"derivedFrom":subQ6}),1.0]])]});}
            var Q51;
            {var subQ5=sQuery(id+"F4.wireOp",EDGE,"E72");Q51=makeQuery(id+"F4.imprint","IMPRINT",FACE,{"disambiguationData":[TD([[makeQuery(id+"F4.imprint","IMPRINT",EDGE,{"derivedFrom":subQ5}),-1.0]])]});}
            var Q52;
            {var subQ0=sQuery(id+"F4.wireOp",EDGE,"E72");Q52=makeQuery(id+"F4.imprint","IMPRINT",FACE,{"disambiguationData":[TD([[makeQuery(id+"F4.imprint","IMPRINT",EDGE,{"derivedFrom":subQ0}),1.0]])]});}
            var Q53;
            {var subQ3=sQuery(id+"F4.wireOp",EDGE,"E73");Q53=makeQuery(id+"F4.imprint","IMPRINT",FACE,{"disambiguationData":[TD([[makeQuery(id+"F4.imprint","IMPRINT",EDGE,{"derivedFrom":subQ3}),-1.0]])]});}
            var Q54;
            {var subQ0=sQuery(id+"F4.wireOp",EDGE,"E68");Q54=makeQuery(id+"F4.imprint","IMPRINT",FACE,{"disambiguationData":[TD([[makeQuery(id+"F4.imprint","IMPRINT",EDGE,{"derivedFrom":subQ0}),-1.0]])]});}
            var Q55;
            {var subQ3=sQuery(id+"F4.wireOp",EDGE,"E69");var subQ5=sQuery(id+"F4.wireOp",EDGE,"E77");var subQ7=makeQuery(id+"F4.imprint","INTERSECT",VERTEX,{"derivedFrom":[subQ3,subQ5]});Q55=makeQuery(id+"F4.imprint","IMPRINT",FACE,{"disambiguationData":[TD([[makeQuery(id+"F4.imprint","IMPRINT",EDGE,{"disambiguationData":[TD([[subQ7,1.0]])],"derivedFrom":subQ3}),1.0]])]});}
            var Q56;
            {var subQ0=sQuery(id+"F4.wireOp",EDGE,"E66");var subQ3=sQuery(id+"F4.wireOp",EDGE,"E75");var subQ5=makeQuery(id+"F4.imprint","INTERSECT",VERTEX,{"derivedFrom":[subQ0,subQ3]});Q56=makeQuery(id+"F4.imprint","IMPRINT",FACE,{"disambiguationData":[TD([[makeQuery(id+"F4.imprint","IMPRINT",EDGE,{"disambiguationData":[TD([[subQ5,-1.0]])],"derivedFrom":subQ3}),-1.0]])]});}
            var Q57;
            {var subQ0=sQuery(id+"F4.wireOp",EDGE,"E71");var subQ3=sQuery(id+"F4.wireOp",EDGE,"E69");var subQ5=makeQuery(id+"F4.imprint","INTERSECT",VERTEX,{"derivedFrom":[subQ3,subQ0]});Q57=makeQuery(id+"F4.imprint","IMPRINT",FACE,{"disambiguationData":[TD([[makeQuery(id+"F4.imprint","IMPRINT",EDGE,{"disambiguationData":[TD([[subQ5,-1.0]])],"derivedFrom":subQ3}),1.0]])]});}
            var Q58;
            {var subQ0=sQuery(id+"F4.wireOp",EDGE,"E67");var subQ3=sQuery(id+"F4.wireOp",EDGE,"E77");var subQ5=makeQuery(id+"F4.imprint","INTERSECT",VERTEX,{"derivedFrom":[subQ0,subQ3]});Q58=makeQuery(id+"F4.imprint","IMPRINT",FACE,{"disambiguationData":[TD([[makeQuery(id+"F4.imprint","IMPRINT",EDGE,{"disambiguationData":[TD([[subQ5,-1.0]])],"derivedFrom":subQ3}),1.0]])]});}
            var Q59;
            {var subQ0=sQuery(id+"F4.wireOp",EDGE,"E77");var subQ1=sQuery(id+"F4.wireOp",EDGE,"E40.left");var subQ2=makeQuery(id+"F4.imprint","INTERSECT",VERTEX,{"derivedFrom":[subQ1,subQ0]});Q59=makeQuery(id+"F4.imprint","IMPRINT",FACE,{"disambiguationData":[TD([[makeQuery(id+"F4.imprint","IMPRINT",EDGE,{"disambiguationData":[TD([[subQ2,1.0]])],"derivedFrom":subQ1}),1.0]])]});}
            var Q60;
            {var subQ0=sQuery(id+"F4.wireOp",EDGE,"E67");var subQ1=sQuery(id+"F4.wireOp",EDGE,"E41.bottom");var subQ2=makeQuery(id+"F4.imprint","INTERSECT",VERTEX,{"derivedFrom":[subQ1,subQ0]});Q60=makeQuery(id+"F4.imprint","IMPRINT",FACE,{"disambiguationData":[TD([[makeQuery(id+"F4.imprint","IMPRINT",EDGE,{"disambiguationData":[TD([[subQ2,-1.0]])],"derivedFrom":subQ1}),-1.0]])]});}
            var Q61;
            {var subQ0=sQuery(id+"F4.wireOp",EDGE,"E68");Q61=makeQuery(id+"F4.imprint","IMPRINT",FACE,{"disambiguationData":[TD([[makeQuery(id+"F4.imprint","IMPRINT",EDGE,{"derivedFrom":subQ0}),1.0]])]});}
            var Q62;
            {var subQ0=sQuery(id+"F4.wireOp",EDGE,"E40.right");var subQ4=sQuery(id+"F4.wireOp",EDGE,"E76");var subQ5=makeQuery(id+"F4.imprint","INTERSECT",VERTEX,{"derivedFrom":[subQ0,subQ4]});Q62=makeQuery(id+"F4.imprint","IMPRINT",FACE,{"disambiguationData":[TD([[makeQuery(id+"F4.imprint","IMPRINT",EDGE,{"disambiguationData":[TD([[subQ5,-1.0]])],"derivedFrom":subQ4}),1.0]])]});}
            extrude(context, id + "F6", {"entities" : qUnion([Q0, Q1, Q2, Q3, Q4, Q5, Q6, Q7, Q8, Q9, Q10, Q11, Q12, Q13, Q14, Q15, Q16, Q17, Q18, Q19, Q20, Q21, Q22, Q23, Q24, Q25, Q26, Q27, Q28, Q29, Q30, Q31, Q32, Q33, Q34, Q35, Q36, Q37, Q38, Q39, Q40, Q41, Q42, Q43, Q44, Q45, Q46, Q47, Q48, Q49, Q50, Q51, Q52, Q53, Q54, Q55, Q56, Q57, Q58, Q59, Q60, Q61, Q62]), "operationType" : NewBodyOperationType.ADD, "depth" : 12 * mm, "offsetDistance" : 25 * mm, "hasSecondDirection" : true, "secondDirectionOppositeDirection" : true, "secondDirectionDepth" : 24 * mm});
        }
        {
            var Q0;
            Q0=makeQuery(id+"F1.opExtrude","SWEPT_FACE",FACE,{"disambiguationData":[OSD([sQuery(id+"F0.wireOp",EDGE,"E0")])]});
            var sketch = newSketch(context, id + "F7", { "sketchPlane" : qUnion([Q0])});
            skLineSegment(sketch, "E78.bottom", {"start": v(-30, -20) * mm, "end": v(0, -20) * mm});
            skLineSegment(sketch, "E78.top", {"start": v(-30, 20) * mm, "end": v(0, 20) * mm});
            skLineSegment(sketch, "E78.left", {"start": v(-30, -20) * mm, "end": v(-30, 20) * mm});
            skLineSegment(sketch, "E78.right", {"start": v(0, -20) * mm, "end": v(0, 20) * mm});
            skLineSegment(sketch, "E79", {"start": v(-30, 0) * mm, "end": v(0, 0) * mm});
            skLineSegment(sketch, "E80", {"start": v(-15, 20) * mm, "end": v(-15, -20) * mm});
            skPoint(sketch, "E81", {"position": v(-15, 0) * mm});
            skSolve(sketch);
        }
        {
            var Q0;
            Q0=sQuery(id+"F7.wireOp",VERTEX,"E81");
            var Q1;
            Q1=makeQuery(id+"F1.opExtrude","SWEPT_BODY",BODY,{"disambiguationData":[OSD([sQuery(id+"F0.wireOp",EDGE,"E0"),sQuery(id+"F0.wireOp",EDGE,"E1"),sQuery(id+"F0.wireOp",EDGE,"E2"),sQuery(id+"F0.wireOp",EDGE,"E3"),sQuery(id+"F0.wireOp",EDGE,"E4"),sQuery(id+"F0.wireOp",EDGE,"E5"),sQuery(id+"F0.wireOp",EDGE,"E6"),sQuery(id+"F0.wireOp",EDGE,"E7"),sQuery(id+"F0.wireOp",EDGE,"E8"),sQuery(id+"F0.wireOp",EDGE,"E9")])]});
            hole(context, id + "F8", {"style" : HoleStyle.C_BORE, "endStyle" : HoleEndStyle.BLIND, "holeDiameter" : 4.5 * mm, "cBoreDiameter" : 9.5 * mm, "cBoreDepth" : 10 * mm, "majorDiameter" : 5 * mm, "holeDepth" : 20 * mm, "isTappedThrough" : true, "tappedDepth" : 12 * mm, "tapClearance" : 3, "startFromSketch" : true, "locations" : qUnion([Q0]), "scope" : qUnion([Q1])});
        }
        {
            var Q0;
            Q0=makeQuery(id+"F1.opExtrude","SWEPT_FACE",FACE,{"disambiguationData":[OSD([sQuery(id+"F0.wireOp",EDGE,"E5")])]});
            var sketch = newSketch(context, id + "F9", { "sketchPlane" : qUnion([Q0])});
            skLineSegment(sketch, "E82.bottom", {"start": v(0, -20) * mm, "end": v(-30, -20) * mm});
            skLineSegment(sketch, "E82.top", {"start": v(0, 20) * mm, "end": v(-30, 20) * mm});
            skLineSegment(sketch, "E82.left", {"start": v(0, -20) * mm, "end": v(0, 20) * mm});
            skLineSegment(sketch, "E82.right", {"start": v(-30, -20) * mm, "end": v(-30, 20) * mm});
            skLineSegment(sketch, "E83", {"start": v(-15, -20) * mm, "end": v(-15, 20) * mm});
            skPoint(sketch, "E84", {"position": v(-15, 0) * mm});
            skSolve(sketch);
        }
        {
            var Q0;
            Q0=sQuery(id+"F9.wireOp",VERTEX,"E84");
            var Q1;
            Q1=makeQuery(id+"F1.opExtrude","SWEPT_BODY",BODY,{"disambiguationData":[OSD([sQuery(id+"F0.wireOp",EDGE,"E0"),sQuery(id+"F0.wireOp",EDGE,"E1"),sQuery(id+"F0.wireOp",EDGE,"E2"),sQuery(id+"F0.wireOp",EDGE,"E3"),sQuery(id+"F0.wireOp",EDGE,"E4"),sQuery(id+"F0.wireOp",EDGE,"E5"),sQuery(id+"F0.wireOp",EDGE,"E6"),sQuery(id+"F0.wireOp",EDGE,"E7"),sQuery(id+"F0.wireOp",EDGE,"E8"),sQuery(id+"F0.wireOp",EDGE,"E9")])]});
            hole(context, id + "F10", {"style" : HoleStyle.C_BORE, "endStyle" : HoleEndStyle.BLIND, "holeDiameter" : 5.5 * mm, "cBoreDiameter" : 9.5 * mm, "cBoreDepth" : 4 * mm, "majorDiameter" : 5 * mm, "holeDepth" : 20 * mm, "isTappedThrough" : true, "tappedDepth" : 12 * mm, "tapClearance" : 3, "startFromSketch" : true, "locations" : qUnion([Q0]), "scope" : qUnion([Q1])});
        }
    });
